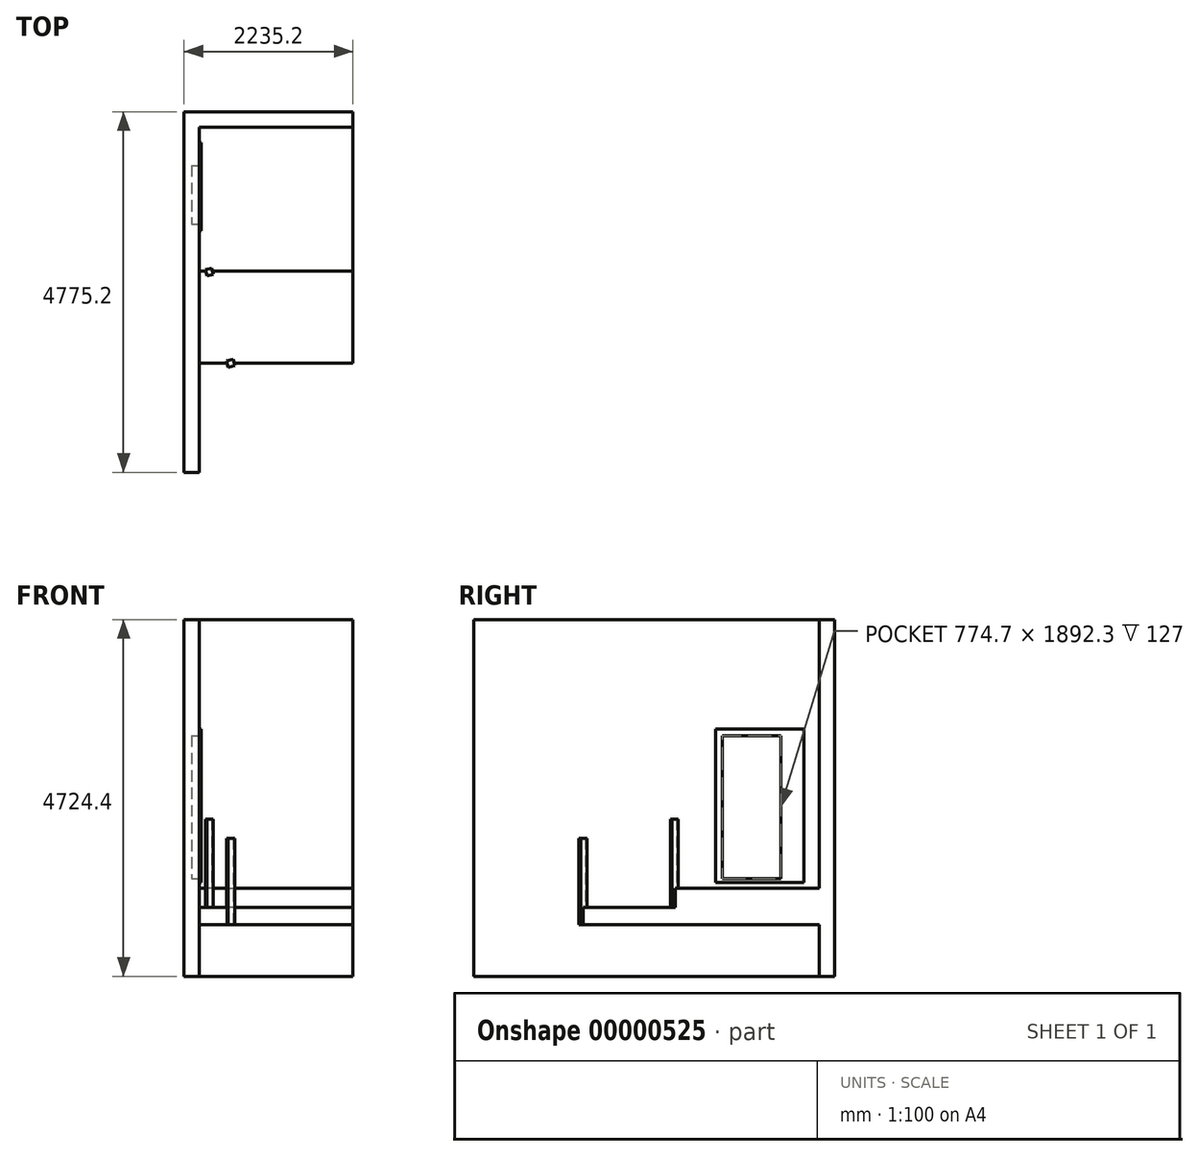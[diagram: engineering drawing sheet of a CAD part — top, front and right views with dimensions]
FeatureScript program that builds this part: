
annotation { "Feature Type Name" : "Feature", "Feature Type Description" : "" }
export const myFeature = defineFeature(function(context is Context, id is Id, definition is map)
    precondition{}
    {
        {
            var Q0;
            Q0=qCreatedBy(makeId("Top.planeOp"),FACE);
            var sketch = newSketch(context, id + "F0", { "sketchPlane" : qUnion([Q0])});
            skLineSegment(sketch, "E0", {"start": v(0, 0) * mm, "end": v(2032, 0) * mm});
            skLineSegment(sketch, "E1", {"start": v(2032, 0) * mm, "end": v(2032, 203.2) * mm});
            skLineSegment(sketch, "E2", {"start": v(2032, 203.2) * mm, "end": v(-203.2, 203.2) * mm});
            skLineSegment(sketch, "E3", {"start": v(-203.2, 203.2) * mm, "end": v(-203.2, -4572) * mm});
            skLineSegment(sketch, "E4", {"start": v(-203.2, -4572) * mm, "end": v(0, -4572) * mm});
            skLineSegment(sketch, "E5", {"start": v(0, -4572) * mm, "end": v(0, 0) * mm});
            skSolve(sketch);
        }
        {
            var Q0;
            Q0=makeQuery(id+"F0.imprint","IMPRINT",FACE,{"disambiguationData":[TD([[makeQuery(id+"F0.imprint","IMPRINT",EDGE,{"derivedFrom":sQuery(id+"F0.wireOp",EDGE,"E0")}),1.0]])]});
            extrude(context, id + "F1", {"entities" : qUnion([Q0]), "depth" : 3810 * mm});
        }
        {
            var Q0;
            Q0=qCreatedBy(makeId("Top.planeOp"),FACE);
            var sketch = newSketch(context, id + "F2", { "sketchPlane" : qUnion([Q0])});
            skLineSegment(sketch, "E6.bottom", {"start": v(0, 0) * mm, "end": v(2032, 0) * mm});
            skLineSegment(sketch, "E6.top", {"start": v(0, -1905) * mm, "end": v(2032, -1905) * mm});
            skLineSegment(sketch, "E6.left", {"start": v(0, 0) * mm, "end": v(0, -1905) * mm});
            skLineSegment(sketch, "E6.right", {"start": v(2032, 0) * mm, "end": v(2032, -1905) * mm});
            skSolve(sketch);
        }
        {
            var Q0;
            Q0=makeQuery(id+"F2.imprint","IMPRINT",FACE,{"disambiguationData":[TD([[makeQuery(id+"F2.imprint","IMPRINT",EDGE,{"derivedFrom":sQuery(id+"F2.wireOp",EDGE,"E6.bottom")}),-1.0]])]});
            extrude(context, id + "F3", {"entities" : qUnion([Q0]), "operationType" : NewBodyOperationType.ADD, "endBound" : BoundingType.SYMMETRIC, "oppositeDirection" : true, "depth" : 457.2 * mm});
        }
        {
            var Q0;
            Q0=makeQuery(id+"F3.opExtrude","SWEPT_FACE",FACE,{"disambiguationData":[OSD([sQuery(id+"F2.wireOp",EDGE,"E6.top")])]});
            var sketch = newSketch(context, id + "F4", { "sketchPlane" : qUnion([Q0])});
            skLineSegment(sketch, "E7.bottom", {"start": v(0, 0) * mm, "end": v(2032, 0) * mm});
            skLineSegment(sketch, "E7.top", {"start": v(0, -228.6) * mm, "end": v(2032, -228.6) * mm});
            skLineSegment(sketch, "E7.left", {"start": v(0, 0) * mm, "end": v(0, -228.6) * mm});
            skLineSegment(sketch, "E7.right", {"start": v(2032, 0) * mm, "end": v(2032, -228.6) * mm});
            skSolve(sketch);
        }
        {
            var Q0;
            Q0=makeQuery(id+"F1.opExtrude","CAP_FACE",FACE,{"disambiguationData":[OSD([sQuery(id+"F0.wireOp",EDGE,"E0"),sQuery(id+"F0.wireOp",EDGE,"E1"),sQuery(id+"F0.wireOp",EDGE,"E2"),sQuery(id+"F0.wireOp",EDGE,"E3"),sQuery(id+"F0.wireOp",EDGE,"E4"),sQuery(id+"F0.wireOp",EDGE,"E5")])],"isStart":true});
            extrude(context, id + "F5", {"entities" : qUnion([Q0]), "operationType" : NewBodyOperationType.ADD, "depth" : 914.4 * mm});
        }
        {
            var Q0;
            Q0=makeQuery(id+"F4.imprint","IMPRINT",FACE,{"disambiguationData":[TD([[makeQuery(id+"F4.imprint","IMPRINT",EDGE,{"derivedFrom":sQuery(id+"F4.wireOp",EDGE,"E7.bottom")}),-1.0]])]});
            extrude(context, id + "F6", {"entities" : qUnion([Q0]), "operationType" : NewBodyOperationType.ADD, "depth" : 1219.2 * mm});
        }
        {
            var Q0;
            {var subQ0=sQuery(id+"F0.wireOp",EDGE,"E5");Q0=makeQuery(id+"F5.boolean.opBoolean","MERGE",FACE,{"derivedFrom":[makeQuery(id+"F1.opExtrude","SWEPT_FACE",FACE,{"disambiguationData":[OSD([subQ0])]}),makeQuery(id+"F5.opExtrude","SWEPT_FACE",FACE,{"disambiguationData":[OSD([subQ0])]})]});}
            var sketch = newSketch(context, id + "F7", { "sketchPlane" : qUnion([Q0])});
            skLineSegment(sketch, "E8.bottom", {"start": v(-1371.6, 2362.2) * mm, "end": v(-203.2, 2362.2) * mm});
            skLineSegment(sketch, "E8.top", {"start": v(-1371.6, 330.2) * mm, "end": v(-203.2, 330.2) * mm});
            skLineSegment(sketch, "E8.left", {"start": v(-1371.6, 2362.2) * mm, "end": v(-1371.6, 330.2) * mm});
            skLineSegment(sketch, "E8.right", {"start": v(-203.2, 2362.2) * mm, "end": v(-203.2, 330.2) * mm});
            skSolve(sketch);
        }
        {
            var Q0;
            Q0=makeQuery(id+"F7.imprint","IMPRINT",FACE,{"disambiguationData":[TD([[makeQuery(id+"F7.imprint","IMPRINT",EDGE,{"derivedFrom":sQuery(id+"F7.wireOp",EDGE,"E8.bottom")}),-1.0]])]});
            extrude(context, id + "F8", {"entities" : qUnion([Q0]), "operationType" : NewBodyOperationType.ADD, "depth" : 25.4 * mm});
        }
        {
            var Q0;
            Q0=makeQuery(id+"F8.opExtrude","CAP_FACE",FACE,{"disambiguationData":[OSD([sQuery(id+"F7.wireOp",EDGE,"E8.bottom"),sQuery(id+"F7.wireOp",EDGE,"E8.top"),sQuery(id+"F7.wireOp",EDGE,"E8.left"),sQuery(id+"F7.wireOp",EDGE,"E8.right")])],"isStart":false});
            var sketch = newSketch(context, id + "F9", { "sketchPlane" : qUnion([Q0])});
            skLineSegment(sketch, "E9", {"start": v(-1282.7, 2273.3) * mm, "end": v(-1282.7, 381) * mm});
            skLineSegment(sketch, "E10", {"start": v(-1282.7, 381) * mm, "end": v(-508, 381) * mm});
            skLineSegment(sketch, "E11", {"start": v(-508, 381) * mm, "end": v(-508, 2273.3) * mm});
            skLineSegment(sketch, "E12", {"start": v(-508, 2273.3) * mm, "end": v(-1282.7, 2273.3) * mm});
            skSolve(sketch);
        }
        {
            var Q0;
            Q0=makeQuery(id+"F9.imprint","IMPRINT",FACE,{"disambiguationData":[TD([[makeQuery(id+"F9.imprint","IMPRINT",EDGE,{"derivedFrom":sQuery(id+"F9.wireOp",EDGE,"E9")}),1.0]])]});
            extrude(context, id + "F10", {"entities" : qUnion([Q0]), "operationType" : NewBodyOperationType.REMOVE, "oppositeDirection" : true, "depth" : 127 * mm});
        }
        {
            var Q0;
            Q0=makeQuery(id+"F3.opExtrude","CAP_FACE",FACE,{"disambiguationData":[OSD([sQuery(id+"F2.wireOp",EDGE,"E6.bottom"),sQuery(id+"F2.wireOp",EDGE,"E6.top"),sQuery(id+"F2.wireOp",EDGE,"E6.left"),sQuery(id+"F2.wireOp",EDGE,"E6.right")])],"isStart":true});
            extrude(context, id + "F11", {"entities" : qUnion([Q0]), "operationType" : NewBodyOperationType.ADD, "depth" : 25.4 * mm});
        }
        {
            var Q0;
            Q0=makeQuery(id+"F11.opExtrude","CAP_FACE",FACE,{"disambiguationData":[OSD([sQuery(id+"F2.wireOp",EDGE,"E6.bottom"),sQuery(id+"F2.wireOp",EDGE,"E6.top"),sQuery(id+"F2.wireOp",EDGE,"E6.left"),sQuery(id+"F2.wireOp",EDGE,"E6.right")])],"isStart":false});
            var sketch = newSketch(context, id + "F12", { "sketchPlane" : qUnion([Q0])});
            skLineSegment(sketch, "E13", {"start": v(25.4, -1270) * mm, "end": v(457.2, -3124.2) * mm, "construction": true});
            skSolve(sketch);
        }
        {
            var Q0;
            Q0=makeQuery(id+"F12.imprint","IMPRINT",FACE,{"disambiguationData":[TD([[makeQuery(id+"F12.imprint","IMPRINT",EDGE,{"derivedFrom":makeQuery(id+"F11.opExtrude","CAP_EDGE",EDGE,{"disambiguationData":[OSD([sQuery(id+"F2.wireOp",EDGE,"E6.top")])],"isStart":false})}),1.0]])]});
            var sketch = newSketch(context, id + "F13", { "sketchPlane" : qUnion([Q0])});
            skLineSegment(sketch, "E14", {"start": v(164.4, -1866.9) * mm, "end": v(77.82, -1887.06) * mm});
            skLineSegment(sketch, "E15", {"start": v(77.82, -1887.06) * mm, "end": v(97.98, -1973.65) * mm});
            skLineSegment(sketch, "E16", {"start": v(97.98, -1973.65) * mm, "end": v(184.57, -1953.48) * mm});
            skLineSegment(sketch, "E17", {"start": v(184.57, -1953.48) * mm, "end": v(164.4, -1866.9) * mm});
            skSolve(sketch);
        }
        {
            var Q0;
            {var subQ5=sQuery(id+"F13.wireOp",EDGE,"E16");Q0=makeQuery(id+"F13.imprint","IMPRINT",FACE,{"disambiguationData":[TD([[makeQuery(id+"F13.imprint","IMPRINT",EDGE,{"derivedFrom":subQ5}),1.0]])]});}
            var Q1;
            Q1=makeQuery(id+"F6.opExtrude","SWEPT_FACE",FACE,{"disambiguationData":[OSD([sQuery(id+"F4.wireOp",EDGE,"E7.bottom")])]});
            extrude(context, id + "F14", {"entities" : qUnion([Q0]), "operationType" : NewBodyOperationType.ADD, "endBound" : BoundingType.UP_TO_SURFACE, "oppositeDirection" : true, "endBoundEntityFace" : qUnion([Q1]), "depth" : 25.4 * mm});
        }
        {
            var Q0;
            {var subQ5=sQuery(id+"F13.wireOp",EDGE,"E16");Q0=makeQuery(id+"F13.imprint","IMPRINT",FACE,{"disambiguationData":[TD([[makeQuery(id+"F13.imprint","IMPRINT",EDGE,{"derivedFrom":subQ5}),1.0]])]});}
            var Q1;
            {var subQ5=sQuery(id+"F13.wireOp",EDGE,"E14");Q1=makeQuery(id+"F13.imprint","IMPRINT",FACE,{"disambiguationData":[TD([[makeQuery(id+"F13.imprint","IMPRINT",EDGE,{"derivedFrom":subQ5}),1.0]])]});}
            extrude(context, id + "F15", {"entities" : qUnion([Q0, Q1]), "operationType" : NewBodyOperationType.ADD, "depth" : 914.4 * mm});
        }
        {
            var Q0;
            Q0=makeQuery(id+"F6.opExtrude","SWEPT_FACE",FACE,{"disambiguationData":[OSD([sQuery(id+"F4.wireOp",EDGE,"E7.bottom")])]});
            var sketch = newSketch(context, id + "F16", { "sketchPlane" : qUnion([Q0])});
            skLineSegment(sketch, "E18", {"start": v(445.68, -3074.72) * mm, "end": v(359.1, -3094.89) * mm});
            skLineSegment(sketch, "E19", {"start": v(359.1, -3094.89) * mm, "end": v(379.26, -3181.47) * mm});
            skLineSegment(sketch, "E20", {"start": v(379.26, -3181.47) * mm, "end": v(465.84, -3161.3) * mm});
            skLineSegment(sketch, "E21", {"start": v(465.84, -3161.3) * mm, "end": v(445.68, -3074.72) * mm});
            skSolve(sketch);
        }
        {
            var Q0;
            {var subQ5=sQuery(id+"F16.wireOp",EDGE,"E20");Q0=makeQuery(id+"F16.imprint","IMPRINT",FACE,{"disambiguationData":[TD([[makeQuery(id+"F16.imprint","IMPRINT",EDGE,{"derivedFrom":subQ5}),1.0]])]});}
            var Q1;
            Q1=makeQuery(id+"F6.boolean.opBoolean","MERGE",FACE,{"derivedFrom":[makeQuery(id+"F3.opExtrude","CAP_FACE",FACE,{"disambiguationData":[OSD([sQuery(id+"F2.wireOp",EDGE,"E6.bottom"),sQuery(id+"F2.wireOp",EDGE,"E6.top"),sQuery(id+"F2.wireOp",EDGE,"E6.left"),sQuery(id+"F2.wireOp",EDGE,"E6.right")])],"isStart":false}),makeQuery(id+"F6.opExtrude","SWEPT_FACE",FACE,{"disambiguationData":[OSD([sQuery(id+"F4.wireOp",EDGE,"E7.top")])]})]});
            extrude(context, id + "F17", {"entities" : qUnion([Q0]), "operationType" : NewBodyOperationType.ADD, "endBound" : BoundingType.UP_TO_SURFACE, "oppositeDirection" : true, "endBoundEntityFace" : qUnion([Q1]), "depth" : 25.4 * mm});
        }
        {
            var Q0;
            {var subQ5=sQuery(id+"F16.wireOp",EDGE,"E20");Q0=makeQuery(id+"F16.imprint","IMPRINT",FACE,{"disambiguationData":[TD([[makeQuery(id+"F16.imprint","IMPRINT",EDGE,{"derivedFrom":subQ5}),1.0]])]});}
            var Q1;
            {var subQ5=sQuery(id+"F16.wireOp",EDGE,"E18");Q1=makeQuery(id+"F16.imprint","IMPRINT",FACE,{"disambiguationData":[TD([[makeQuery(id+"F16.imprint","IMPRINT",EDGE,{"derivedFrom":subQ5}),1.0]])]});}
            extrude(context, id + "F18", {"entities" : qUnion([Q0, Q1]), "operationType" : NewBodyOperationType.ADD, "depth" : 914.4 * mm});
        }
    });
